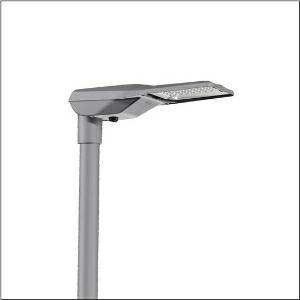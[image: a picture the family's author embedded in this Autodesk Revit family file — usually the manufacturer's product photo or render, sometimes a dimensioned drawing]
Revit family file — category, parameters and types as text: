
# Revit family: streetlight_sl_21_iq_mini___st1_0a_5xe2d31u08hb_e98e
name_source: partatom
category: Lighting Fixtures
units: mm (PartAtom-declared; Revit-internal decimal feet)

## family parameters
Cut with Voids When Loaded = No
Host = Face
Light Source = No
Part Type = Normal
Room Calculation Point = No
Round Connector Dimension = Use Diameter
Shared = No

## types (1)
- --- (1 x LED, 9750 lm, 71 W, 3000K)
    Apparent Load = 71 VA
    CIE Flux Codes = 37 72 97 100 100
    Color Rendering = 70
    Color Temperature = 3000K
    Default Elevation = 1800 mm
    Description = Streetlight SL 21 iQ mini, mast luminaire, primary light control with lens, of PMMA, primary optical cover: cover, of toughened safety glass, transparent, light distribution: ST1.0a, light emission: direct distribution, primary light characteristic: asymmetric, installation type: post-top, side-entry, LED, High Power LED, rated luminous flux: 9.750lm, luminous efficacy: 137lm/W, light colour: 730, colour temperature: 3000K, control gear: iQ-Street Remote, D4i with power reduction, control: pre-setting: logarithmic dimming characteristic, Street-Remote, Auto-Match, Temp-Guard, Lumen-Switch, Night-Set, Smart-Wire, Light-Fading, Desk-Remote (wireless, voltage-free reading and setting of iQ features in the workshop via application-optimized NFC function/RFID function), optimised constant luminous flux control (CLO 2.0), mains connection: 220..240V, AC, 50/60Hz, start of lifetime: 71W, end of service life: 75W, reduction: 30W, luminaire housing, of diecast aluminium, powder-coated, SITECO metallic grey (DB 702S), corrosivity category C5 high according to DIN EN ISO 12944, please order mast flange separately, inclination adjustable: 0°, 5°, 10°, 15°, sealing non-destructively replaceable, multi-level sealing system, length: 628mm, width: 235mm, height: 110mm, mast flange for spigot size: 42mm (side-entry): 5XC10008XM4, 60/48mm (side-entry/post-top): 5XC10108XM2, 76/60mm (side-entry/post-top): 5XC10108XM1, mounting height: 4..8m, Smart Interface below, protection rating (complete): IP66, insulation class (complete): insulation class II (safety insulation), certification: CE, ENEC, ENEC+, VDE, impact resistance: IK10, permissible operating ambient temperature for outdoor applications: -40..+50°C, standard-compliant lighting for roads and squares, packaging unit: 1 piece

Light Distribution: ST1.0a
    Height = 110 mm
    Lamp = 1 x LED
    Lamp Light Flux = 9750 lm
    Lamp Power = 71 W
    Lamp count = 1
    Length = 625 mm
    Luminous efficacy = 137 lm/W
    Manufacturer = Siteco
    ModVariant = No
    Model = 5XE2D31U08HB
    Number of Poles = 1
    OnlyDefault = Yes
    Power Factor = 1
    Product Name = Streetlight SL 21 iQ mini | ST1.0a
    Product group = mast luminaire | pylon top
    ProductGroupID = 6100
    Protection Class = Protection class II
    Protection Degree = IP 66
    RLX_Detail_Level = 1
    RLX_Emergency_Light_Flux = 0 lm
    RLX_Emergency_Type = 0
    RLX_Emergency_Type_DB = No
    RlxData = <blob elided: 94589 chars, md5=e13dda85>
    Socket = socket
    Standby Power = 0 W
    System Light Flux = 9750 lm
    System Power = 71 W
    Type Comments = factory setting: luminous flux: 100 % | dim-lin: 254 | 716 mA
    Type Image = l_1003516.jpg
    URL = http://relux.com
    VarID = @adj_115311
    Voltage = 0 V
    Weight = 0.00 kg
    Width = 234 mm

## geometry (parser evidence)
native form markers: Blend x4, Sweep x10
no freeform markers — native parametric forms only
